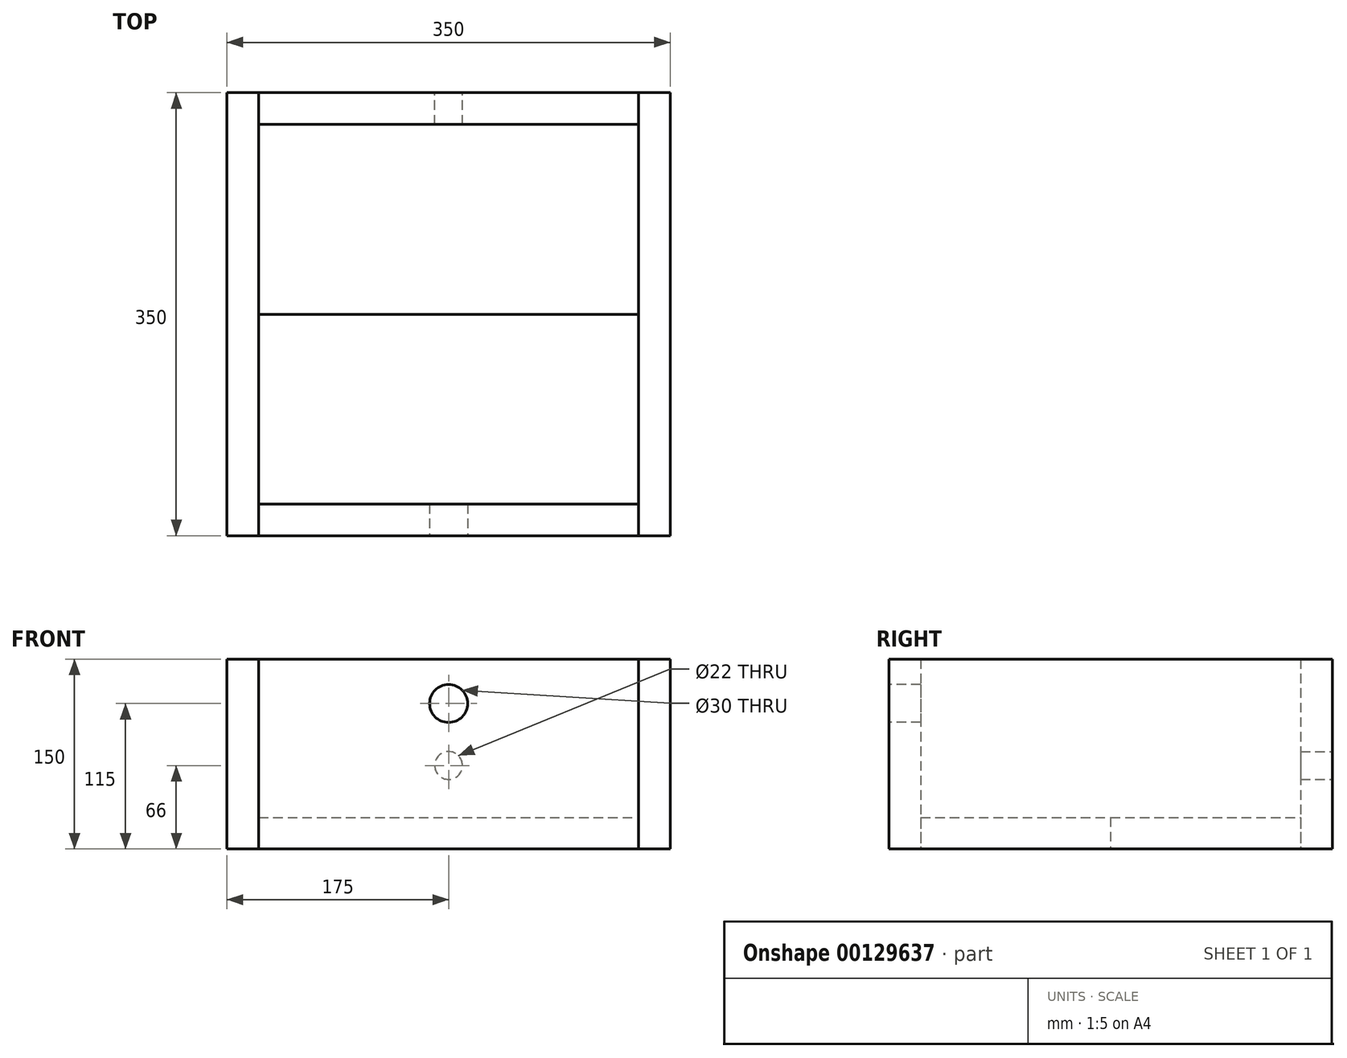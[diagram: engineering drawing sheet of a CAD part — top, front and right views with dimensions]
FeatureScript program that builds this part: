
annotation { "Feature Type Name" : "Feature", "Feature Type Description" : "" }
export const myFeature = defineFeature(function(context is Context, id is Id, definition is map)
    precondition{}
    {
        {
            var Q0;
            Q0=qCreatedBy(makeId("Top.planeOp"),FACE);
            var sketch = newSketch(context, id + "F0", { "sketchPlane" : qUnion([Q0])});
            skLineSegment(sketch, "E0.bottom", {"start": v(0, 0) * mm, "end": v(300, 0) * mm});
            skLineSegment(sketch, "E0.top", {"start": v(0, 150) * mm, "end": v(300, 150) * mm});
            skLineSegment(sketch, "E0.left", {"start": v(0, 0) * mm, "end": v(0, 150) * mm});
            skLineSegment(sketch, "E0.right", {"start": v(300, 0) * mm, "end": v(300, 150) * mm});
            skLineSegment(sketch, "E1.top", {"start": v(0, 300) * mm, "end": v(300, 300) * mm});
            skLineSegment(sketch, "E1.left", {"start": v(0, 150) * mm, "end": v(0, 300) * mm});
            skLineSegment(sketch, "E1.right", {"start": v(300, 150) * mm, "end": v(300, 300) * mm});
            skLineSegment(sketch, "E2.top", {"start": v(0, -25) * mm, "end": v(300, -25) * mm});
            skLineSegment(sketch, "E2.left", {"start": v(0, 0) * mm, "end": v(0, -25) * mm});
            skLineSegment(sketch, "E2.right", {"start": v(300, 0) * mm, "end": v(300, -25) * mm});
            skLineSegment(sketch, "E3.top", {"start": v(0, 325) * mm, "end": v(300, 325) * mm});
            skLineSegment(sketch, "E3.left", {"start": v(0, 300) * mm, "end": v(0, 325) * mm});
            skLineSegment(sketch, "E3.right", {"start": v(300, 300) * mm, "end": v(300, 325) * mm});
            skLineSegment(sketch, "E4.bottom", {"start": v(300, 325) * mm, "end": v(325, 325) * mm});
            skLineSegment(sketch, "E4.top", {"start": v(300, -25) * mm, "end": v(325, -25) * mm});
            skLineSegment(sketch, "E4.left", {"start": v(300, 325) * mm, "end": v(300, -25) * mm});
            skLineSegment(sketch, "E4.right", {"start": v(325, 325) * mm, "end": v(325, -25) * mm});
            skLineSegment(sketch, "E5.bottom", {"start": v(0, 325) * mm, "end": v(-25, 325) * mm});
            skLineSegment(sketch, "E5.top", {"start": v(0, -25) * mm, "end": v(-25, -25) * mm});
            skLineSegment(sketch, "E5.left", {"start": v(0, 325) * mm, "end": v(0, -25) * mm});
            skLineSegment(sketch, "E5.right", {"start": v(-25, 325) * mm, "end": v(-25, -25) * mm});
            skSolve(sketch);
        }
        {
            var Q0;
            {var subQ0=sQuery(id+"F0.wireOp",EDGE,"E0.top");Q0=makeQuery(id+"F0.imprint","IMPRINT",FACE,{"disambiguationData":[TD([[makeQuery(id+"F0.imprint","IMPRINT",EDGE,{"derivedFrom":subQ0}),-1.0]])]});}
            extrude(context, id + "F1", {"entities" : qUnion([Q0]), "depth" : 25 * mm});
        }
        {
            var Q0;
            {var subQ0=sQuery(id+"F0.wireOp",EDGE,"E0.top");Q0=makeQuery(id+"F0.imprint","IMPRINT",FACE,{"disambiguationData":[TD([[makeQuery(id+"F0.imprint","IMPRINT",EDGE,{"derivedFrom":subQ0}),1.0]])]});}
            extrude(context, id + "F2", {"entities" : qUnion([Q0]), "depth" : 25 * mm});
        }
        {
            var Q0;
            {var subQ0=sQuery(id+"F0.wireOp",EDGE,"E1.top");Q0=makeQuery(id+"F0.imprint","IMPRINT",FACE,{"disambiguationData":[TD([[makeQuery(id+"F0.imprint","IMPRINT",EDGE,{"derivedFrom":subQ0}),1.0]])]});}
            var Q1;
            {var subQ0=sQuery(id+"F0.wireOp",EDGE,"E0.bottom");Q1=makeQuery(id+"F0.imprint","IMPRINT",FACE,{"disambiguationData":[TD([[makeQuery(id+"F0.imprint","IMPRINT",EDGE,{"derivedFrom":subQ0}),-1.0]])]});}
            extrude(context, id + "F3", {"entities" : qUnion([Q0, Q1]), "depth" : 150 * mm});
        }
        {
            var Q0;
            {var subQ3=sQuery(id+"F0.wireOp",EDGE,"E4.bottom");Q0=makeQuery(id+"F0.imprint","IMPRINT",FACE,{"disambiguationData":[TD([[makeQuery(id+"F0.imprint","IMPRINT",EDGE,{"derivedFrom":subQ3}),-1.0]])]});}
            var Q1;
            {var subQ3=sQuery(id+"F0.wireOp",EDGE,"E5.bottom");Q1=makeQuery(id+"F0.imprint","IMPRINT",FACE,{"disambiguationData":[TD([[makeQuery(id+"F0.imprint","IMPRINT",EDGE,{"derivedFrom":subQ3}),1.0]])]});}
            extrude(context, id + "F4", {"entities" : qUnion([Q0, Q1]), "depth" : 150 * mm});
        }
        {
            var Q0;
            Q0=makeQuery(id+"F3.opExtrude","SWEPT_FACE",FACE,{"disambiguationData":[OSD([sQuery(id+"F0.wireOp",EDGE,"E3.top")])]});
            var sketch = newSketch(context, id + "F5", { "sketchPlane" : qUnion([Q0])});
            skLineSegment(sketch, "E6.0", {"start": v(0, 66) * mm, "end": v(-300, 66) * mm});
            skCircle(sketch, "E7", {"center": v(-150, 66) * mm, "radius": 11 * mm});
            skSolve(sketch);
        }
        {
            var Q0;
            Q0 = qSketchRegion(id + "F5", true);
            var Q1;
            Q1=makeQuery(id+"F3.opExtrude","SWEPT_FACE",FACE,{"disambiguationData":[OSD([sQuery(id+"F0.wireOp",EDGE,"E1.top")])]});
            extrude(context, id + "F6", {"entities" : qUnion([Q0]), "operationType" : NewBodyOperationType.REMOVE, "endBound" : BoundingType.UP_TO_SURFACE, "oppositeDirection" : true, "endBoundEntityFace" : qUnion([Q1]), "depth" : 25 * mm});
        }
        {
            var Q0;
            Q0=makeQuery(id+"F3.opExtrude","SWEPT_FACE",FACE,{"disambiguationData":[OSD([sQuery(id+"F0.wireOp",EDGE,"E2.top")])]});
            var sketch = newSketch(context, id + "F7", { "sketchPlane" : qUnion([Q0])});
            skCircle(sketch, "E8", {"center": v(150, 115) * mm, "radius": 15 * mm});
            skSolve(sketch);
        }
        {
            var Q0;
            Q0 = qSketchRegion(id + "F7", true);
            var Q1;
            Q1=makeQuery(id+"F3.opExtrude","SWEPT_FACE",FACE,{"disambiguationData":[OSD([sQuery(id+"F0.wireOp",EDGE,"E0.bottom")])]});
            extrude(context, id + "F8", {"entities" : qUnion([Q0]), "operationType" : NewBodyOperationType.REMOVE, "endBound" : BoundingType.UP_TO_SURFACE, "oppositeDirection" : true, "endBoundEntityFace" : qUnion([Q1]), "depth" : 25 * mm});
        }
    });
